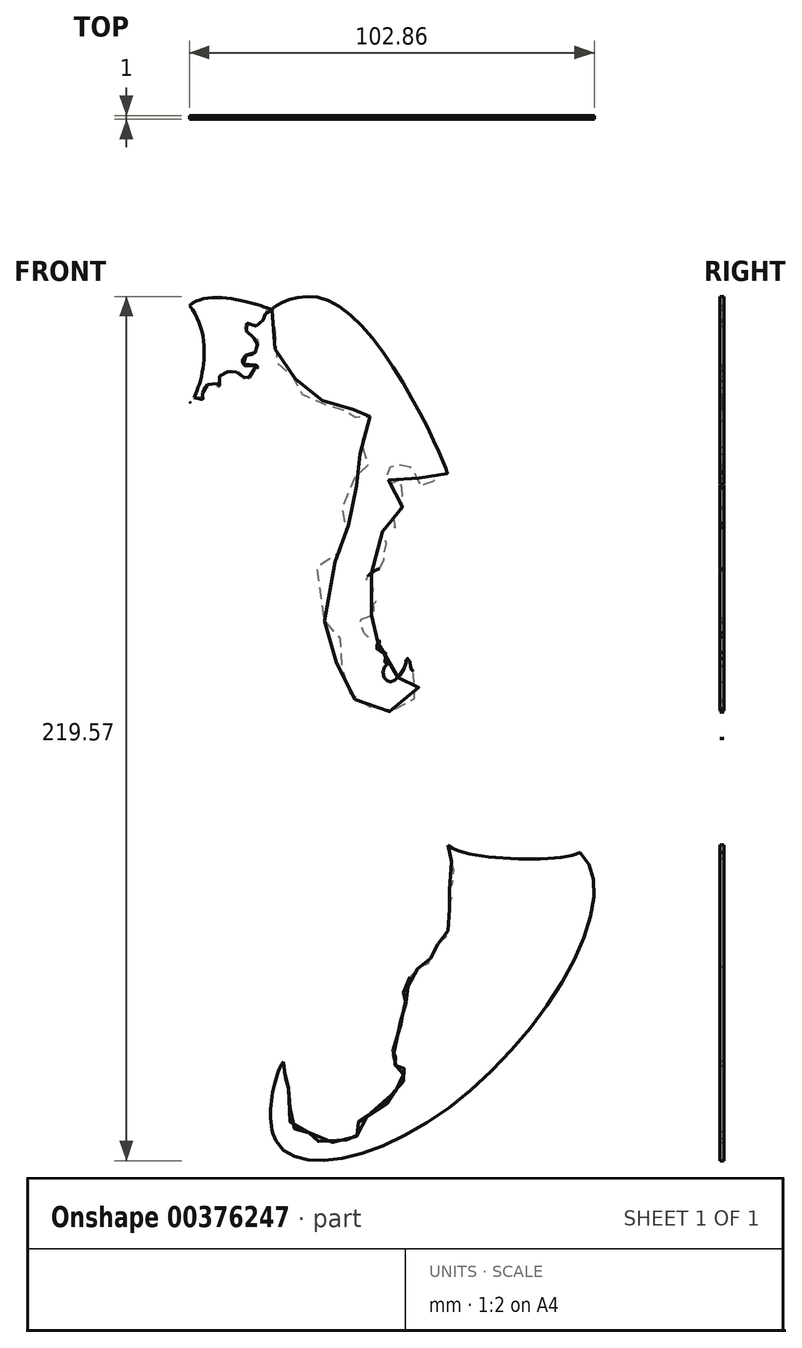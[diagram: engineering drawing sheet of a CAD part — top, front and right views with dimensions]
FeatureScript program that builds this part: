
annotation { "Feature Type Name" : "Feature", "Feature Type Description" : "" }
export const myFeature = defineFeature(function(context is Context, id is Id, definition is map)
    precondition{}
    {
        {
            var Q0;
            Q0=qCreatedBy(makeId("Front.planeOp"),FACE);
            var sketch = newSketch(context, id + "F0", { "sketchPlane" : qUnion([Q0])});
            skFitSpline(sketch, "E0", {"points": [v(-1.02, 104.12) * mm, v(-2.2, 104.24) * mm, v(-2.62, 102.82) * mm, v(-2.8, 101.46) * mm, v(-3.5, 101.46) * mm, v(-4.87, 99.92) * mm, v(-5.4, 100.5) * mm, v(-7.06, 100.86) * mm, v(-8.07, 99.68) * mm, v(-7.3, 98.5) * mm, v(-6.41, 97.55) * mm, v(-4.75, 96.54) * mm, v(-4.52, 95.59) * mm, v(-5.1, 94.1) * mm, v(-5.23, 93.46) * mm, v(-6.31, 92.8) * mm, v(-7.6, 92.56) * mm, v(-8.49, 91.2) * mm, v(-7.55, 89.91) * mm, v(-4.9, 90.03) * mm, v(-4.78, 89.26) * mm, v(-5.43, 89.09) * mm, v(-6.37, 87.09) * mm, v(-7.02, 86.85) * mm, v(-7.72, 86.32) * mm, v(-8.25, 87.15) * mm, v(-9.6, 88.38) * mm, v(-10.08, 88.38) * mm, v(-10.49, 88.8) * mm, v(-12.66, 88.32) * mm, v(-13.55, 87.85) * mm, v(-14.72, 86.56) * mm, v(-14.37, 84.97) * mm, v(-14.6, 84.26) * mm, v(-14.9, 84.85) * mm, v(-15.6, 85.8) * mm, v(-17.37, 85.09) * mm, v(-18.67, 83.97) * mm, v(-18.43, 81.9) * mm, v(-18.31, 81.32) * mm, v(-18.84, 81.44) * mm, v(-19.31, 81.85) * mm, v(-21.49, 81.38) * mm, v(-21.84, 80.62) * mm, v(-22, 105.2) * mm, v(-1.02, 104.12) * mm]});
            skFitSpline(sketch, "E1", {"points": [v(-21.84, 80.62) * mm, v(-22.68, 81.87) * mm, v(-24.63, 82.62) * mm, v(-29.47, 83.15) * mm, v(-30.02, 82.37) * mm, v(-30.54, 83.23) * mm, v(-30.38, 83.61) * mm, v(-31.7, 84.28) * mm, v(-31.7, 85.16) * mm, v(-31.7, 85.77) * mm, v(-32.59, 86.93) * mm, v(-31.26, 86.77) * mm, v(-29.66, 86.82) * mm, v(-29.1, 87.43) * mm, v(-29.33, 88.43) * mm, v(-30.32, 88.92) * mm, v(-30.49, 89.31) * mm, v(-31.93, 89.37) * mm, v(-31.6, 90.3) * mm, v(-32.92, 91.1) * mm, v(-35.22, 88.21) * mm, v(-35.77, 88) * mm, v(-35.83, 87.33) * mm, v(-35.44, 87.33) * mm, v(-35.33, 86.73) * mm, v(-36.88, 86.5) * mm, v(-38.09, 85.8) * mm, v(-38.42, 83.26) * mm, v(-38.75, 83.15) * mm, v(-38.86, 83.48) * mm, v(-41.6, 84.7) * mm, v(-41.94, 85.3) * mm, v(-42.21, 85.85) * mm, v(-45.02, 86.78) * mm, v(-45.35, 87.66) * mm, v(-50.08, 88.21) * mm, v(-51.24, 89.26) * mm, v(-52.5, 89.92) * mm, v(-54.97, 89.59) * mm, v(-54.3, 90.14) * mm, v(-54.3, 93.6) * mm, v(-55.96, 94.49) * mm, v(-56.9, 95.15) * mm, v(-58.05, 95.26) * mm, v(-57.61, 96.2) * mm, v(-59.48, 97.62) * mm, v(-60.42, 97.3) * mm, v(-61.68, 97.9) * mm, v(-62.67, 98.4) * mm, v(-64.66, 99) * mm, v(-64.55, 99.77) * mm, v(-66.14, 102.41) * mm, v(-67.68, 102.96) * mm, v(-67.07, 104) * mm, v(-68.36, 106.06) * mm, v(-68.6, 109.36) * mm, v(-69.54, 110.3) * mm, v(-71.14, 113.66) * mm, v(-70.84, 114.73) * mm, v(-71.73, 115.67) * mm, v(-22, 105.2) * mm, v(-21.84, 80.62) * mm]});
            skFitSpline(sketch, "E2", {"points": [v(-1.02, 104.12) * mm, v(-0.43, 103.93) * mm, v(0.26, 103.06) * mm, v(0.36, 102.54) * mm, v(0.52, 102.33) * mm, v(0.33, 101.57) * mm, v(0.3, 100.63) * mm, v(0.2, 99.83) * mm, v(0.18, 99.44) * mm, v(-0.39, 97.53) * mm, v(-0.14, 97.11) * mm, v(0.08, 96.6) * mm, v(-0.42, 95.19) * mm, v(-0.24, 94.54) * mm, v(-0.2, 92.1) * mm, v(0.22, 91.65) * mm, v(0.17, 90.67) * mm, v(0.5, 90.14) * mm, v(0.64, 89.6) * mm, v(1.46, 89.6) * mm, v(2.18, 89.41) * mm, v(2.76, 88.5) * mm, v(2.76, 87.73) * mm, v(3.18, 87.29) * mm, v(4.1, 87.29) * mm, v(4.77, 86.96) * mm, v(5.03, 86.51) * mm, v(5.8, 86.02) * mm, v(6.37, 84.57) * mm, v(5.43, 82.5) * mm, v(5.78, 82.12) * mm, v(6.16, 82.53) * mm, v(7.14, 82.62) * mm, v(8.3, 81.62) * mm, v(8.61, 81.38) * mm, v(9.94, 81.47) * mm, v(10.53, 81.15) * mm, v(10.83, 81.2) * mm, v(11.66, 81.15) * mm, v(12.37, 80.05) * mm, v(12.62, 80.12) * mm, v(12.7, 80.44) * mm, v(13.4, 81.15) * mm, v(14.4, 81.22) * mm, v(14.83, 80.76) * mm, v(15.5, 80.8) * mm, v(16, 80.44) * mm, v(16.47, 79.9) * mm, v(16.6, 78.87) * mm, v(18.14, 79.48) * mm, v(19, 79.58) * mm, v(19.63, 78.98) * mm, v(19.63, 77.79) * mm, v(19.96, 76.93) * mm, v(19.96, 76) * mm, v(20.24, 76.32) * mm, v(20.29, 77.07) * mm, v(21.32, 77.77) * mm, v(21.7, 78.28) * mm, v(22.63, 79.17) * mm, v(24.4, 79.08) * mm, v(25.02, 78.24) * mm, v(24.64, 77.26) * mm, v(23.75, 76.93) * mm, v(23.66, 76.37) * mm, v(22.72, 75.38) * mm, v(22.96, 74.96) * mm, v(23.05, 71.69) * mm, v(22.72, 71.4) * mm, v(23.05, 70.75) * mm, v(20.38, 69.82) * mm, v(19.87, 69.3) * mm, v(20.66, 69.25) * mm, v(20.76, 67.66) * mm, v(21.32, 67.48) * mm, v(22.3, 67.38) * mm, v(23.38, 65.06) * mm, v(22.16, 63.5) * mm, v(19.83, 63.56) * mm, v(19.83, 63.18) * mm, v(18.3, 61.92) * mm, v(18.9, 61.69) * mm, v(19.13, 61.31) * mm, v(19.7, 61.55) * mm, v(20.63, 59.86) * mm, v(19.65, 58.65) * mm, v(17.93, 57.01) * mm, v(17.4, 55.49) * mm, v(16.46, 53.96) * mm, v(16.75, 53.71) * mm, v(17.59, 53.9) * mm, v(19.56, 53.66) * mm, v(20.02, 51.84) * mm, v(18.5, 50.31) * mm, v(18.44, 49.45) * mm, v(17.73, 47.77) * mm, v(17.98, 47.42) * mm, v(18.7, 47.06) * mm, v(19.66, 45.95) * mm, v(19.15, 44.4) * mm, v(17.27, 43.88) * mm, v(17.02, 43.43) * mm, v(15.8, 42.3) * mm, v(15.04, 42.05) * mm, v(15.23, 41.34) * mm, v(14.73, 39.67) * mm, v(12.7, 38.14) * mm, v(11.68, 37.94) * mm, v(10.39, 38.6) * mm, v(9.88, 38.6) * mm, v(9.83, 36.51) * mm, v(10.54, 30.8) * mm, v(12.06, 25.14) * mm, v(12.44, 25.2) * mm, v(12.92, 25.68) * mm, v(14.6, 25.58) * mm, v(14.97, 24.6) * mm, v(15.3, 24.6) * mm, v(16.23, 23.83) * mm, v(16.56, 21.32) * mm, v(15.96, 19.69) * mm, v(16.34, 18.05) * mm, v(16.22, 15.82) * mm, v(15.16, 13.92) * mm, v(15.33, 13.53) * mm, v(15.94, 13.75) * mm, v(17.34, 12.85) * mm, v(18.5, 11.9) * mm, v(18.69, 10.37) * mm, v(17.68, 9.17) * mm, v(17.87, 8.35) * mm, v(18.6, 7.73) * mm, v(18.74, 6.9) * mm, v(19.6, 6.38) * mm, v(20.32, 4.84) * mm, v(20.66, 5.18) * mm, v(21.43, 4.7) * mm, v(21.86, 4.8) * mm, v(22.78, 3.64) * mm, v(23.11, 3.25) * mm, v(24.22, 3.3) * mm, v(25.37, 4.36) * mm, v(26.58, 4.4) * mm, v(27.78, 3.01) * mm, v(27.78, 2.58) * mm, v(28.36, 2.63) * mm, v(29.03, 2) * mm, v(29.37, 2.3) * mm, v(30.38, 2.44) * mm, v(30.66, 2.24) * mm, v(31.1, 2.58) * mm, v(32.44, 2.39) * mm, v(32.88, 2.77) * mm, v(33.84, 2.97) * mm, v(33.89, 3.6) * mm, v(35.23, 5.42) * mm, v(35.33, 6.33) * mm, v(35.33, 6.9) * mm, v(36.24, 8.02) * mm, v(36.1, 8.64) * mm, v(36.05, 9.22) * mm, v(35.19, 10.47) * mm, v(35.04, 12.06) * mm, v(34.66, 12.49) * mm, v(34.18, 13.02) * mm, v(34.13, 14.46) * mm, v(33.36, 15.57) * mm, v(33.02, 15.13) * mm, v(33.07, 14.65) * mm, v(31.96, 11.96) * mm, v(29.51, 9.7) * mm, v(28.4, 9.9) * mm, v(27.35, 11.05) * mm, v(27.54, 13.26) * mm, v(28.21, 14.03) * mm, v(27.63, 14.65) * mm, v(27.92, 16.96) * mm, v(27.1, 17.1) * mm, v(25.52, 18.3) * mm, v(26.29, 19.8) * mm, v(26.54, 19.9) * mm, v(25.72, 20.57) * mm, v(25.6, 22.06) * mm, v(25.22, 21.44) * mm, v(22.7, 21.4) * mm, v(22.03, 23.13) * mm, v(21.74, 23.4) * mm, v(21.45, 24.17) * mm, v(21.7, 25.5) * mm, v(23.62, 26.22) * mm, v(24.9, 27.25) * mm, v(24.94, 28.38) * mm, v(24.94, 29.6) * mm, v(25.5, 30.12) * mm, v(24.74, 30.72) * mm, v(24.42, 32.05) * mm, v(24.7, 32.58) * mm, v(24.62, 33.9) * mm, v(23.92, 34.2) * mm, v(23.03, 35.64) * mm, v(23.55, 36.68) * mm, v(26.16, 38.31) * mm, v(26.5, 38.27) * mm, v(27.33, 39.37) * mm, v(27.52, 40.9) * mm, v(28.2, 42.04) * mm, v(27.9, 42.42) * mm, v(27.4, 43.03) * mm, v(27.44, 44.08) * mm, v(28.16, 44.84) * mm, v(27.82, 45.04) * mm, v(26.92, 47.36) * mm, v(27.67, 48.63) * mm, v(27.94, 49.05) * mm, v(28.5, 49.65) * mm, v(29.52, 49.61) * mm, v(30.35, 48.82) * mm, v(30.3, 49.16) * mm, v(29.93, 50.4) * mm, v(29.97, 51.84) * mm, v(30.3, 52.19) * mm, v(30.76, 52.3) * mm, v(31.03, 52.71) * mm, v(32.5, 53.58) * mm, v(32.17, 54) * mm, v(32.17, 55.54) * mm, v(32.62, 55.92) * mm, v(32.32, 56.15) * mm, v(32.47, 57.32) * mm, v(32.7, 57.62) * mm, v(31.94, 59.13) * mm, v(31.94, 60.16) * mm, v(31.68, 60.39) * mm, v(31.38, 60.99) * mm, v(31.11, 60.39) * mm, v(29.76, 59.93) * mm, v(28.75, 60.27) * mm, v(28.52, 61.32) * mm, v(28.07, 62) * mm, v(28.28, 63.25) * mm, v(29.27, 64.35) * mm, v(30.39, 64.5) * mm, v(30.76, 64.76) * mm, v(31.77, 64.87) * mm, v(33.34, 64.35) * mm, v(33.83, 64.35) * mm, v(34.58, 63.94) * mm, v(34.99, 62.78) * mm, v(36.7, 60.9) * mm, v(36.7, 59.52) * mm, v(37.27, 58.81) * mm, v(37.5, 59.27) * mm, v(38.25, 60.05) * mm, v(38.78, 59.87) * mm, v(39, 60.25) * mm, v(40.12, 60.7) * mm, v(40.24, 61.23) * mm, v(41.1, 61.97) * mm, v(41.7, 62.83) * mm, v(42.96, 62.98) * mm, v(43.53, 62.6) * mm, v(13.79, 106.34) * mm, v(-1.02, 104.12) * mm]});
            skFitSpline(sketch, "E3", {"points": [v(43.53, 62.6) * mm, v(44.05, 62.73) * mm, v(45.2, 62.02) * mm, v(45.57, 60.22) * mm, v(45.56, 60.12) * mm, v(45.8, 60.18) * mm, v(46.89, 59.01) * mm, v(47.1, 59.14) * mm, v(47.33, 59.14) * mm, v(47.4, 59.67) * mm, v(48.04, 60.4) * mm, v(48.64, 60.43) * mm, v(49.12, 60.88) * mm, v(49.1, 61.53) * mm, v(49.86, 62.42) * mm, v(50.8, 62.6) * mm, v(50.9, 63.38) * mm, v(50.86, 64.16) * mm, v(52.42, 65.4) * mm, v(52.28, 65.76) * mm, v(52.02, 66.22) * mm, v(52.24, 67.15) * mm, v(53.04, 67.4) * mm, v(53.75, 67.44) * mm, v(53.97, 67.26) * mm, v(54.83, 67.22) * mm, v(55.56, 66.74) * mm, v(55.8, 66.76) * mm, v(56.2, 66.63) * mm, v(56.38, 67.03) * mm, v(58.38, 68.31) * mm, v(60, 68.3) * mm, v(60.37, 67.9) * mm, v(60.21, 67.67) * mm, v(60.55, 67.67) * mm, v(61.46, 67.16) * mm, v(61.8, 67.23) * mm, v(63.12, 66.34) * mm, v(63.18, 65.04) * mm, v(63.47, 64.75) * mm, v(63.27, 63.38) * mm, v(62.27, 62.38) * mm, v(62.74, 62.45) * mm, v(63.71, 62.3) * mm, v(64.95, 61.05) * mm, v(65.64, 59.04) * mm, v(65.22, 58.53) * mm, v(65.62, 58.44) * mm, v(66.28, 59.04) * mm, v(67.52, 58.97) * mm, v(68.14, 58.35) * mm, v(68.19, 56.84) * mm, v(67.54, 56.33) * mm, v(67.72, 55.85) * mm, v(67.67, 53.71) * mm, v(67.88, 53.69) * mm, v(68.66, 55.14) * mm, v(69.24, 55.37) * mm, v(69.33, 53.73) * mm, v(68.78, 53.3) * mm, v(68.75, 52.6) * mm, v(67.58, 52.38) * mm, v(67.1, 52.6) * mm, v(66.91, 52.01) * mm, v(66.62, 51.76) * mm, v(66.13, 52.01) * mm, v(64.8, 51.99) * mm, v(64.32, 52.24) * mm, v(64.2, 51.57) * mm, v(63.2, 50.42) * mm, v(63.37, 50.05) * mm, v(64, 49.7) * mm, v(64.4, 49.08) * mm, v(64.34, 48.03) * mm, v(63.66, 47.42) * mm, v(62.45, 47.32) * mm, v(62.14, 47.6) * mm, v(61.77, 47.44) * mm, v(60.43, 47.3) * mm, v(60.32, 47.05) * mm, v(59.37, 46.71) * mm, v(58.8, 45.96) * mm, v(57.75, 44.55) * mm, v(58.09, 42.64) * mm, v(58.1, 41.87) * mm, v(58.87, 41) * mm, v(59.43, 40.92) * mm, v(64.75, 37.19) * mm, v(64.87, 35.56) * mm, v(65.23, 35.96) * mm, v(65.8, 35.9) * mm, v(66.68, 35.25) * mm, v(66.1, 34.86) * mm, v(65.46, 34.97) * mm, v(65.32, 34.66) * mm, v(66, 34.32) * mm, v(67.42, 29.99) * mm, v(66.54, 25.84) * mm, v(66.07, 25.06) * mm, v(65.94, 23.3) * mm, v(65.53, 22.23) * mm, v(65.58, 19.56) * mm, v(65.3, 17.44) * mm, v(64.94, 16.57) * mm, v(63.17, 13.95) * mm, v(62.89, 13.4) * mm, v(62.97, 12.6) * mm, v(63.45, 12.3) * mm, v(64.2, 11.88) * mm, v(65.48, 10) * mm, v(65.78, 7.67) * mm, v(65.7, 7) * mm, v(66.13, 6.55) * mm, v(66.98, 3.94) * mm, v(67.12, 1.96) * mm, v(67.4, 1.9) * mm, v(67.97, 1.18) * mm, v(68.15, 0.23) * mm, v(68.25, 0.22) * mm, v(68.78, 0.2) * mm, v(69.55, -0.99) * mm, v(70.4, -1.82) * mm, v(71.23, -1.84) * mm, v(72.78, -2.97) * mm, v(72.95, -2.95) * mm, v(73.72, -3.01) * mm, v(74.16, -3.66) * mm, v(74.8, -3.72) * mm, v(75.66, -3.7) * mm, v(76.67, -4.78) * mm, v(69.93, 73.3) * mm, v(48.97, 70.67) * mm, v(43.53, 62.6) * mm]});
            skFitSpline(sketch, "E4", {"points": [v(76.67, -4.78) * mm, v(76.82, -5.02) * mm, v(76.8, -6.42) * mm, v(75.49, -7.57) * mm, v(75.4, -7.59) * mm, v(75.76, -7.84) * mm, v(75.73, -8.86) * mm, v(75.82, -9.14) * mm, v(76.14, -9.3) * mm, v(76.45, -9.7) * mm, v(76.54, -10.71) * mm, v(77.86, -12.8) * mm, v(78.17, -13.03) * mm, v(78.09, -14.52) * mm, v(77.64, -14.84) * mm, v(76.67, -16.2) * mm, v(76.52, -17.29) * mm, v(76.2, -17.54) * mm, v(75.93, -18.34) * mm, v(76.49, -18.92) * mm, v(76.53, -20.04) * mm, v(76.92, -20.19) * mm, v(77.22, -22.79) * mm, v(75.62, -23.96) * mm, v(74.76, -23.79) * mm, v(74.63, -24.32) * mm, v(74.35, -25.4) * mm, v(73.5, -25.92) * mm, v(73.6, -26.24) * mm, v(72.26, -27.47) * mm, v(70.59, -27.67) * mm, v(69.93, -26.75) * mm, v(69.8, -25.9) * mm, v(69.49, -25.49) * mm, v(69.22, -23.7) * mm, v(68.75, -23.6) * mm, v(67.66, -21.8) * mm, v(67.77, -20.55) * mm, v(67.43, -20.27) * mm, v(66.8, -19.04) * mm, v(66.14, -17.76) * mm, v(66.08, -16.25) * mm, v(65.53, -15.35) * mm, v(65.7, -14) * mm, v(65.65, -13.66) * mm, v(64.8, -12.85) * mm, v(64.76, -12.29) * mm, v(63.9, -12.25) * mm, v(62.24, -10.61) * mm, v(62.27, -8.9) * mm, v(62.02, -8.58) * mm, v(61.94, -6.26) * mm, v(64, -5.48) * mm, v(65.44, -4.31) * mm, v(65.3, -4.1) * mm, v(63.48, -5.02) * mm, v(61.74, -5.72) * mm, v(59.28, -5.7) * mm, v(58.17, -4.6) * mm, v(55.1, -3.04) * mm, v(54.59, -3.21) * mm, v(52.78, -6.52) * mm, v(52.77, -8.23) * mm, v(52.44, -10.24) * mm, v(52.7, -10.67) * mm, v(52.78, -11.6) * mm, v(51.89, -12.38) * mm, v(50.73, -12.22) * mm, v(50.73, -12.69) * mm, v(50.35, -14.5) * mm, v(48.92, -15.65) * mm, v(48.4, -16.94) * mm, v(48.07, -17.7) * mm, v(47.97, -18.5) * mm, v(47.2, -19.36) * mm, v(46.92, -19.8) * mm, v(47.26, -20.56) * mm, v(45.69, -25.27) * mm, v(44.54, -26.13) * mm, v(44.4, -26.65) * mm, v(44.83, -27.23) * mm, v(44.64, -28.04) * mm, v(45.07, -28.8) * mm, v(43.77, -31.77) * mm, v(77.27, -33.73) * mm, v(79.12, -25.18) * mm, v(79.98, -6.96) * mm, v(76.67, -4.78) * mm]});
            skFitSpline(sketch, "E5", {"points": [v(43.77, -31.77) * mm, v(44.27, -33.67) * mm, v(44.13, -34.2) * mm, v(44.44, -34.52) * mm, v(44.44, -35.68) * mm, v(45, -37.1) * mm, v(44.52, -42.4) * mm, v(44.1, -42.96) * mm, v(44.55, -44.35) * mm, v(44.64, -45.42) * mm, v(44, -46.78) * mm, v(44.1, -48.6) * mm, v(43.55, -51.94) * mm, v(44.01, -52.2) * mm, v(43.95, -53.38) * mm, v(42.9, -54.05) * mm, v(42.9, -54.22) * mm, v(43.12, -54.42) * mm, v(43.12, -55.34) * mm, v(41.15, -57.03) * mm, v(40.93, -57.26) * mm, v(41.04, -57.59) * mm, v(40.13, -58.58) * mm, v(39.34, -60.05) * mm, v(39.14, -61.4) * mm, v(37.39, -62.81) * mm, v(36.77, -62.7) * mm, v(36.6, -63.05) * mm, v(35.82, -63.38) * mm, v(35.55, -63.87) * mm, v(34.15, -65.29) * mm, v(34.12, -65.7) * mm, v(33.1, -68.38) * mm, v(31.96, -70.03) * mm, v(32.28, -70.5) * mm, v(32.78, -71.11) * mm, v(33.16, -72.27) * mm, v(33.09, -73.82) * mm, v(31.55, -75.86) * mm, v(31.45, -76.36) * mm, v(31.73, -76.84) * mm, v(31.8, -77.31) * mm, v(30.62, -78.87) * mm, v(30.67, -80.07) * mm, v(30.8, -81.58) * mm, v(30.26, -83.7) * mm, v(29.6, -84.1) * mm, v(29.84, -84.41) * mm, v(29.86, -85.15) * mm, v(30.2, -85.46) * mm, v(30.26, -86.3) * mm, v(29.45, -87.51) * mm, v(29.8, -87.6) * mm, v(30.63, -87.93) * mm, v(31.26, -87.82) * mm, v(32.12, -88) * mm, v(32.58, -88.94) * mm, v(32.34, -89.71) * mm, v(32.5, -91.03) * mm, v(31.48, -93.45) * mm, v(30.28, -93.83) * mm, v(30.33, -94.32) * mm, v(30.44, -95.12) * mm, v(29.66, -96.37) * mm, v(21.28, -102) * mm, v(21, -102.21) * mm, v(21.24, -102.5) * mm, v(20.86, -105.19) * mm, v(19.49, -106.31) * mm, v(18.48, -106.34) * mm, v(18.2, -106.63) * mm, v(12.5, -107.42) * mm, v(9.16, -106.37) * mm, v(9.16, -105.65) * mm, v(7.73, -104.66) * mm, v(6, -104.6) * mm, v(4.43, -103.62) * mm, v(3.56, -101.7) * mm, v(3.8, -94.2) * mm, v(3.5, -93.76) * mm, v(3.05, -93.5) * mm, v(2.48, -92.16) * mm, v(2.25, -91.86) * mm, v(2.48, -90.56) * mm, v(2.2, -89.51) * mm, v(2.03, -89.01) * mm, v(2.13, -87.99) * mm, v(2.83, -87.54) * mm, v(2.73, -86.94) * mm, v(1.96, -86.91) * mm, v(0, -107) * mm, v(45.5, -97.4) * mm, v(77.27, -33.73) * mm, v(43.77, -31.77) * mm]});
            skFitSpline(sketch, "E6", {"points": [v(1.96, -86.91) * mm, v(-0.39, -87.97) * mm, v(-3.16, -90.12) * mm, v(-4.93, -90.93) * mm, v(-6.37, -92.88) * mm, v(-6.45, -94.55) * mm, v(-7.15, -94.32) * mm, v(-7.85, -94.18) * mm, v(-7.85, -93.14) * mm, v(-8, -92.22) * mm, v(-7.33, -91.63) * mm, v(-7.33, -91.15) * mm, v(-7.85, -91.08) * mm, v(-8.26, -91.7) * mm, v(-8.34, -92.13) * mm, v(-9.02, -92.29) * mm, v(-9.88, -90.91) * mm, v(-9.7, -89.83) * mm, v(-9.78, -89.13) * mm, v(-10.2, -89.5) * mm, v(-12.64, -89.88) * mm, v(-13.1, -90.15) * mm, v(-13.34, -89.94) * mm, v(-12.91, -89.64) * mm, v(-12.53, -88.15) * mm, v(-12.24, -88.04) * mm, v(-11.83, -88.48) * mm, v(-11.61, -88.07) * mm, v(-11.32, -87.8) * mm, v(-12.07, -87.8) * mm, v(-12.07, -87.34) * mm, v(-12.34, -87.18) * mm, v(-11.67, -86.64) * mm, v(-12.07, -85.56) * mm, v(-13.05, -85.56) * mm, v(-13.26, -85.64) * mm, v(-13.67, -85.83) * mm, v(-14.75, -85.56) * mm, v(-15.05, -84.64) * mm, v(-14.3, -84.48) * mm, v(-14.3, -84.07) * mm, v(-13.8, -84.02) * mm, v(-13.32, -84.2) * mm, v(-12.91, -84.12) * mm, v(-12.7, -82.7) * mm, v(-11.67, -82.7) * mm, v(-10.91, -84.45) * mm, v(-10.5, -84.64) * mm, v(-10.24, -85.12) * mm, v(-9.83, -85.12) * mm, v(-8.5, -86.29) * mm, v(-6, -87.72) * mm, v(-5.67, -88.13) * mm, v(-5.1, -88.02) * mm, v(-3.75, -86.53) * mm, v(-3.04, -84.96) * mm, v(-2.45, -84.45) * mm, v(-1.64, -84.58) * mm, v(-1.34, -85.45) * mm, v(-0.77, -85.56) * mm, v(-0.42, -85.29) * mm, v(0.23, -85.18) * mm, v(0.2, -84.64) * mm, v(0.2, -84.1) * mm, v(0.74, -83.85) * mm, v(1.53, -83.7) * mm, v(2.18, -83.85) * mm, v(2.34, -83.3) * mm, v(1.45, -82.8) * mm, v(1.58, -82.16) * mm, v(2.74, -80.75) * mm, v(3.15, -80.83) * mm, v(3.77, -80.3) * mm, v(5.07, -80.21) * mm, v(6.31, -80.54) * mm, v(6.9, -81.54) * mm, v(6.9, -82.62) * mm, v(7.18, -82.78) * mm, v(7.48, -82.3) * mm, v(8.45, -81.8) * mm, v(8.34, -81.54) * mm, v(8.42, -80.32) * mm, v(8.06, -79.89) * mm, v(7.72, -78.15) * mm, v(7.21, -77.54) * mm, v(6.87, -76.08) * mm, v(6.6, -75.87) * mm, v(5.37, -75.16) * mm, v(5.03, -73.8) * mm, v(4.59, -73.83) * mm, v(3.33, -73.01) * mm, v(3.2, -73.83) * mm, v(2.27, -74.65) * mm, v(0.37, -75.53) * mm, v(-5.05, -74.82) * mm, v(-7.84, -72.33) * mm, v(-8.18, -69.78) * mm, v(-20.29, -87.77) * mm, v(0, -107) * mm], "startDerivative": vector(-149.08, -50.47) * mm, "endDerivative": vector(621.95, -305.66) * mm});
            skFitSpline(sketch, "E7", {"points": [v(-8.18, -69.78) * mm, v(-9.32, -69.23) * mm, v(-9.28, -68.7) * mm, v(-9.76, -68.35) * mm, v(-10.11, -68.4) * mm, v(-11.74, -66.77) * mm, v(-11.74, -65.67) * mm, v(-12.75, -64.4) * mm, v(-13.19, -62.9) * mm, v(-13.14, -61.23) * mm, v(-12.4, -60.4) * mm, v(-11.91, -60.44) * mm, v(-11.08, -59.69) * mm, v(-11.03, -59.07) * mm, v(-10.46, -58.5) * mm, v(-9.55, -58.46) * mm, v(-9.16, -57.8) * mm, v(-8.72, -57.18) * mm, v(-9.16, -56.48) * mm, v(-10.56, -55.3) * mm, v(-11.88, -52.4) * mm, v(-11.62, -48.61) * mm, v(-10.8, -46.9) * mm, v(-9.61, -46.47) * mm, v(-8.95, -46.03) * mm, v(-9.87, -45.99) * mm, v(-11.62, -46.03) * mm, v(-13.24, -44.85) * mm, v(-13.9, -43.32) * mm, v(-13.71, -43) * mm, v(-14.38, -43.07) * mm, v(-15.39, -42.14) * mm, v(-15.1, -39.5) * mm, v(-15.78, -39.44) * mm, v(-16.48, -38.04) * mm, v(-16.48, -37) * mm, v(-16.89, -36.83) * mm, v(-19.37, -36.06) * mm, v(-20.3, -34.83) * mm, v(-20.2, -30.93) * mm, v(-20.3, -30.63) * mm, v(-20.77, -30.9) * mm, v(-21.8, -30.8) * mm, v(-22.5, -30.17) * mm, v(-23.13, -28.94) * mm, v(-23.46, -28.9) * mm, v(-28, -29.83) * mm, v(-30.8, -30) * mm, v(-31.88, -29.33) * mm, v(-31.68, -30) * mm, v(-31.45, -30.79) * mm, v(-31.75, -31.77) * mm, v(-32.68, -31.77) * mm, v(-32.38, -30.26) * mm, v(-33.54, -29.23) * mm, v(-34, -29.96) * mm, v(-34.57, -29.76) * mm, v(-36.98, -28) * mm, v(-37.61, -27.08) * mm, v(-38.1, -27.16) * mm, v(-41.97, -27.72) * mm, v(-42.97, -26.72) * mm, v(-44.44, -27.03) * mm, v(-45.06, -26.88) * mm, v(-45.22, -25.97) * mm, v(-46.25, -25.7) * mm, v(-47.1, -24.66) * mm, v(-20.29, -87.77) * mm], "startDerivative": vector(-116.36, 33.3) * mm, "endDerivative": vector(405.18, -945.68) * mm});
            skFitSpline(sketch, "E8", {"points": [v(-47.1, -24.66) * mm, v(-47.96, -25.04) * mm, v(-49.05, -22.9) * mm, v(-49.74, -22.58) * mm, v(-50.51, -21.8) * mm, v(-52.38, -21.03) * mm, v(-54.43, -21.4) * mm, v(-54.52, -21.94) * mm, v(-55.75, -22.49) * mm, v(-57.57, -21.99) * mm, v(-58.16, -20.53) * mm, v(-56.48, -18.2) * mm, v(-56.43, -17.62) * mm, v(-57.98, -16.8) * mm, v(-59.12, -17.84) * mm, v(-63.9, -17.3) * mm, v(-65.13, -14.29) * mm, v(-65.86, -13.83) * mm, v(-66.54, -13.52) * mm, v(-66.64, -12.88) * mm, v(-73.06, -8.49) * mm, v(-73.33, -8.76) * mm, v(-75.52, -7.3) * mm, v(-75.65, -5.9) * mm, v(-76.48, -5.73) * mm, v(-83.07, -0.42) * mm, v(-83.29, 2.44) * mm, v(-82.58, 3.85) * mm, v(-83.46, 5.9) * mm, v(-84.83, 14.67) * mm, v(-83.96, 15.94) * mm, v(-84.9, 15.9) * mm, v(-85.42, 16.54) * mm, v(-86.87, 16.45) * mm, v(-86.53, 15.42) * mm, v(-87.38, 15.3) * mm, v(-87.51, 14.87) * mm, v(-88.15, 15.12) * mm, v(-87.77, 15.77) * mm, v(-87.77, 16.66) * mm, v(-86.49, 17.7) * mm, v(-84.56, 18) * mm, v(-85.46, 18.68) * mm, v(-88.27, 25.59) * mm, v(-87.97, 26.27) * mm, v(-88.1, 27.73) * mm, v(-87.41, 28.37) * mm, v(-87.24, 29.87) * mm, v(-88.8, 33.22) * mm, v(-88.68, 35.15) * mm, v(-87.1, 37.67) * mm, v(-87.13, 38.13) * mm, v(-86.53, 39.15) * mm, v(-85.47, 39.32) * mm, v(-84.92, 39.83) * mm, v(-84.32, 40.04) * mm, v(-83.25, 42.81) * mm, v(-82.87, 43.58) * mm, v(-84.02, 43.45) * mm, v(-85.68, 44.47) * mm, v(-86.67, 46.65) * mm, v(-86.53, 48.3) * mm, v(-85.51, 49.24) * mm, v(-85.92, 50.46) * mm, v(-86.6, 51.43) * mm, v(-86.08, 53.37) * mm, v(-84.3, 55.96) * mm, v(-83.11, 55.75) * mm, v(-82.44, 56.93) * mm, v(-82.17, 57.84) * mm, v(-81.54, 57.52) * mm, v(-81.14, 57.72) * mm, v(-81.02, 59.14) * mm, v(-79.52, 61.3) * mm, v(-79.6, 61.98) * mm, v(-78.38, 62.8) * mm, v(-76.44, 64.04) * mm, v(-76.04, 65.37) * mm, v(-75.06, 66.23) * mm, v(-73.33, 65.96) * mm, v(-72.99, 65.57) * mm, v(-72.9, 66.83) * mm, v(-73.03, 68.38) * mm, v(-71.52, 68.77) * mm, v(-69.83, 69.47) * mm, v(-68.23, 71.1) * mm, v(-66.98, 73.31) * mm, v(-67.45, 74.1) * mm, v(-67.2, 75.56) * mm, v(-66.24, 76.3) * mm, v(-65.9, 77.33) * mm, v(-64.95, 79.02) * mm, v(-64.86, 81.79) * mm, v(-64.18, 83.44) * mm, v(-65.55, 85.57) * mm, v(-65.29, 86.73) * mm, v(-65.33, 90.32) * mm, v(-66.14, 90.9) * mm, v(-67.94, 94.15) * mm, v(-69.22, 94.58) * mm, v(-70.63, 97.36) * mm, v(-70.25, 101.36) * mm, v(-70.25, 101.94) * mm, v(-71.2, 102.1) * mm, v(-72.04, 102.74) * mm, v(-71.96, 104.21) * mm, v(-72.64, 105) * mm, v(-72.88, 105.73) * mm, v(-75.47, 107.6) * mm, v(-75.59, 111.98) * mm, v(-75.35, 112.54) * mm, v(-76.46, 113.45) * mm, v(-76.7, 114.85) * mm, v(-71.73, 115.67) * mm], "startDerivative": vector(-136.56, -123.58) * mm, "endDerivative": vector(427.29, 8.75) * mm});
            skSolve(sketch);
        }
        {
            var Q0;
            {var subQ0=sQuery(id+"F0.wireOp",EDGE,"E1");var subQ1=sQuery(id+"F0.wireOp",EDGE,"E0");var subQ2=makeQuery(id+"F0.imprint","INTERSECT",VERTEX,{"disambiguationData":[OD(2.0)],"derivedFrom":[subQ1,subQ0]});Q0=makeQuery(id+"F0.imprint","IMPRINT",FACE,{"disambiguationData":[TD([[makeQuery(id+"F0.imprint","IMPRINT",EDGE,{"disambiguationData":[TD([[subQ2,-1.0]])],"derivedFrom":subQ1}),-1.0]])]});}
            var Q1;
            {var subQ0=sQuery(id+"F0.wireOp",EDGE,"E2");var subQ1=sQuery(id+"F0.wireOp",EDGE,"E0");var subQ2=makeQuery(id+"F0.imprint","INTERSECT",VERTEX,{"disambiguationData":[OD(1.0)],"derivedFrom":[subQ1,subQ0]});Q1=makeQuery(id+"F0.imprint","IMPRINT",FACE,{"disambiguationData":[TD([[makeQuery(id+"F0.imprint","IMPRINT",EDGE,{"disambiguationData":[TD([[subQ2,-1.0]])],"derivedFrom":subQ1}),-1.0]])]});}
            var Q2;
            {var subQ0=sQuery(id+"F0.wireOp",EDGE,"E2");var subQ1=sQuery(id+"F0.wireOp",EDGE,"E0");var subQ2=makeQuery(id+"F0.imprint","INTERSECT",VERTEX,{"disambiguationData":[OD(0.0)],"derivedFrom":[subQ1,subQ0]});Q2=makeQuery(id+"F0.imprint","IMPRINT",FACE,{"disambiguationData":[TD([[makeQuery(id+"F0.imprint","IMPRINT",EDGE,{"disambiguationData":[TD([[subQ2,-1.0]])],"derivedFrom":subQ1}),1.0]])]});}
            var Q3;
            {var subQ0=sQuery(id+"F0.wireOp",EDGE,"E3");var subQ1=sQuery(id+"F0.wireOp",EDGE,"E2");var subQ2=makeQuery(id+"F0.imprint","INTERSECT",VERTEX,{"disambiguationData":[OD(0.0)],"derivedFrom":[subQ1,subQ0]});Q3=makeQuery(id+"F0.imprint","IMPRINT",FACE,{"disambiguationData":[TD([[makeQuery(id+"F0.imprint","IMPRINT",EDGE,{"disambiguationData":[TD([[subQ2,-1.0]])],"derivedFrom":subQ1}),-1.0]])]});}
            var Q4;
            {var subQ0=sQuery(id+"F0.wireOp",EDGE,"E4");var subQ1=sQuery(id+"F0.wireOp",EDGE,"E3");var subQ2=makeQuery(id+"F0.imprint","INTERSECT",VERTEX,{"disambiguationData":[OD(0.0)],"derivedFrom":[subQ1,subQ0]});Q4=makeQuery(id+"F0.imprint","IMPRINT",FACE,{"disambiguationData":[TD([[makeQuery(id+"F0.imprint","IMPRINT",EDGE,{"disambiguationData":[TD([[subQ2,-1.0]])],"derivedFrom":subQ0}),1.0]])]});}
            extrude(context, id + "F1", {"entities" : qUnion([Q0, Q1, Q2, Q3, Q4]), "depth" : 1 * mm});
        }
        {
            var Q0;
            {var subQ0=sQuery(id+"F0.wireOp",EDGE,"E5");var subQ1=sQuery(id+"F0.wireOp",EDGE,"E4");var subQ2=makeQuery(id+"F0.imprint","INTERSECT",VERTEX,{"disambiguationData":[OD(0.0)],"derivedFrom":[subQ1,subQ0]});Q0=makeQuery(id+"F0.imprint","IMPRINT",FACE,{"disambiguationData":[TD([[makeQuery(id+"F0.imprint","IMPRINT",EDGE,{"disambiguationData":[TD([[subQ2,1.0]])],"derivedFrom":subQ1}),-1.0]])]});}
            extrude(context, id + "F2", {"entities" : qUnion([Q0]), "depth" : 1 * mm});
        }
    });
